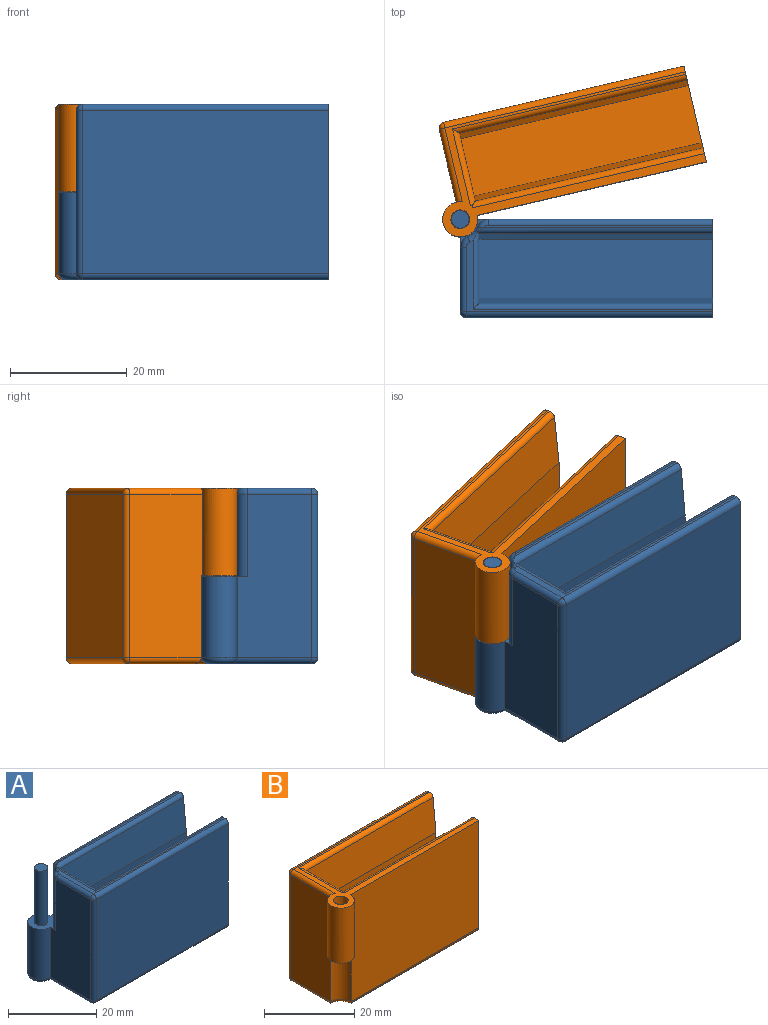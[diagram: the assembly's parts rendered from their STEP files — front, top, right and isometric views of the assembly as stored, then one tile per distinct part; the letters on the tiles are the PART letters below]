
ASSEMBLY  parts=2 mates=1
PART A: 36 faces, bbox 46.4x20x30 mm
  f0: plane 39.23x0.45mm, normal (0,0,1), area 17.3mm2, adj f7,f25,f27,f28
  f1: cylinder r=3.2mm len=14.05mm, axis (0,0,-1), area 35.1mm2, adj f13,f16,f17,f26
  f2: plane 28x12.8mm, normal (-1,0,0), area 333.1mm2, adj f12,f13,f16,f22,f32,f34
  f3: plane 42.2x28mm, normal (0,-1,0), area 1181.6mm2, adj f7,f20,f31,f34
  f4: plane 40x15mm, normal (0,1,0), area 600mm2, adj f5,f7,f11,f18
  f5: plane 24x11.9mm, normal (1,0,0), area 250.5mm2, adj f4,f6,f11,f18,f19,f23
  f6: plane 40x15mm, normal (0,-1,0), area 600mm2, adj f5,f7,f11,f19
  f7: plane 30x16.8mm, normal (1,0,0), area 240.3mm2, adj f0,f3,f4,f6,f8,f9,f10,f11
  f8: plane 40.2x28mm, normal (0,1,0), area 1100.3mm2, adj f7,f12,f13,f17,f28,f29
  f9: plane 42.2x12.22mm, normal (0,0,1), area 32.5mm2, adj f7,f20,f21,f22,f23,f24,f26
  f10: plane 45.2x17.8mm, normal (0,0,-1), area 636.8mm2, adj f7,f29,f30,f31,f32
  f11: plane 40x10.1mm, normal (0,0,1), area 404mm2, adj f4,f5,f6,f7
  f12: cylinder r=3mm len=13.95mm, axis (0,0,-1), area 197.2mm2, adj f2,f8,f13,f30
  f13: plane 7.8x7.8mm, normal (0,0,1), area 23mm2, adj f1,f2,f8,f12,f15,f16,f17
  f14: plane 3x3mm, normal (0,0,1), area 7.1mm2, adj f15
  f15: cylinder r=1.5mm len=15.05mm, axis (0,0,-1), area 141.8mm2, adj f13,f14
  f16: cylinder r=2mm len=14.05mm, axis (0,0,-1), area 33mm2, adj f1,f2,f13,f24
  f17: cylinder r=2mm len=14.05mm, axis (0,0,-1), area 33mm2, adj f1,f8,f13,f27
  f18: plane 40.01x9.1mm, normal (0,1,0.1), area 365.8mm2, adj f4,f5,f7,f21,f23
  f19: plane 40.01x9.1mm, normal (0,-1,0.1), area 365.8mm2, adj f5,f6,f7,f23,f25
  f20: cylinder r=1mm len=42.2mm, axis (-1,0,0), area 66.3mm2, adj f3,f7,f9,f35
  f21: cylinder r=1mm len=41mm, axis (1,0,0), area 59.4mm2, adj f7,f9,f18,f23
  f22: cylinder r=1mm len=11mm, axis (0,1,0), area 17.3mm2, adj f2,f9,f24,f35
  f23: cylinder r=1mm len=13.25mm, axis (0,-1,0), area 19.1mm2, adj f5,f9,f18,f19,f21,f25,f26
  f24: torus R=1mm, axis (0,0,1), area 3mm2, adj f9,f16,f22,f26
  f25: cylinder r=1mm len=40.34mm, axis (-1,0,0), area 58.8mm2, adj f0,f7,f19,f23,f26,f27
  f26: torus R=4.2mm, axis (0,0,1), area 3.4mm2, adj f1,f9,f23,f24,f25,f27
  f27: torus R=1mm, axis (0,0,1), area 3mm2, adj f0,f17,f25,f26,f28
  f28: cylinder r=1mm len=38.4mm, axis (1,0,0), area 60.3mm2, adj f0,f7,f8,f27
  f29: cylinder r=1mm len=41.47mm, axis (-1,0,0), area 63.8mm2, adj f7,f8,f10,f30
  f30: torus R=2mm, axis (0,0,1), area 20.7mm2, adj f10,f12,f29,f32
  f31: cylinder r=1mm len=42.2mm, axis (1,0,0), area 66.3mm2, adj f3,f7,f10,f33
  f32: cylinder r=1mm len=14.07mm, axis (0,-1,0), area 20.8mm2, adj f2,f10,f30,f33
  f33: sphere r=1mm, area 1.6mm2, adj f31,f32,f34
  f34: cylinder r=1mm len=28mm, axis (0,0,-1), area 44mm2, adj f2,f3,f33,f35
  f35: sphere r=1mm, area 1.6mm2, adj f20,f22,f34
PART B: 29 faces, bbox 46.2x19.8x30 mm
  f0: plane 30x16.8mm, normal (1,0,0), area 240.5mm2, adj f1,f7,f10,f11,f13,f14,f15,f16
  f1: plane 46.2x18.8mm, normal (0,0,1), area 112.7mm2, adj f0,f3,f4,f6,f7,f8,f18,f19
  f2: cylinder r=3.2mm len=14.05mm, axis (0,0,-1), area 70.6mm2, adj f5,f9,f22,f28
  f3: cylinder r=3mm len=0.59mm, axis (0,0,-1), area 0mm2, adj f1,f7,f8
  f4: cylinder r=3mm len=14.95mm, axis (0,0,-1), area 211.6mm2, adj f1,f5,f9,f19,f28
  f5: plane 6.2x6.2mm, normal (0,0,-1), area 21.2mm2, adj f2,f4,f6,f9,f28
  f6: cylinder r=1.6mm len=14.95mm, axis (0,0,-1), area 150.3mm2, adj f1,f5
  f7: cylinder r=1mm len=40.74mm, axis (-1,0,0), area 59.4mm2, adj f0,f1,f3,f8,f17
  f8: cylinder r=1mm len=13.65mm, axis (0,1,0), area 19.8mm2, adj f1,f3,f7,f12,f16,f17,f18
  f9: plane 28x12.8mm, normal (-1,0,0), area 355.6mm2, adj f2,f4,f5,f19,f24,f26
  f10: plane 42.2x28mm, normal (0,1,0), area 1181.6mm2, adj f0,f20,f23,f26
  f11: plane 40x15mm, normal (0,-1,0), area 600mm2, adj f0,f12,f15,f16
  f12: plane 24x11.9mm, normal (1,0,0), area 250.5mm2, adj f8,f11,f13,f15,f16,f17
  f13: plane 40x15mm, normal (0,1,0), area 600mm2, adj f0,f12,f15,f17
  f14: plane 42.2x14.8mm, normal (0,0,-1), area 618mm2, adj f0,f21,f22,f23,f24
  f15: plane 40x10.1mm, normal (0,0,1), area 404mm2, adj f0,f11,f12,f13
  f16: plane 40.01x9.1mm, normal (0,-1,0.1), area 365.8mm2, adj f0,f8,f11,f12,f18
  f17: plane 40.01x9.1mm, normal (0,1,0.1), area 365.8mm2, adj f0,f7,f8,f12,f13
  f18: cylinder r=1mm len=41mm, axis (1,0,0), area 59.4mm2, adj f0,f1,f8,f16
  f19: cylinder r=1mm len=12.97mm, axis (0,-1,0), area 20.2mm2, adj f1,f4,f9,f27
  f20: cylinder r=1mm len=42.2mm, axis (-1,0,0), area 66.3mm2, adj f0,f1,f10,f27
  f21: cylinder r=1mm len=40mm, axis (-1,0,0), area 62.3mm2, adj f0,f14,f22,f28
  f22: torus R=4.2mm, axis (0,0,1), area 7.6mm2, adj f2,f14,f21,f24
  f23: cylinder r=1mm len=42.2mm, axis (1,0,0), area 66.3mm2, adj f0,f10,f14,f25
  f24: cylinder r=1mm len=12.6mm, axis (0,1,0), area 19.3mm2, adj f9,f14,f22,f25
  f25: sphere r=1mm, area 1.6mm2, adj f23,f24,f26
  f26: cylinder r=1mm len=28mm, axis (0,0,-1), area 44mm2, adj f9,f10,f25,f27
  f27: sphere r=1mm, area 1.6mm2, adj f19,f20,f26
  f28: plane 40.2x29mm, normal (0,-1,0), area 1163mm2, adj f0,f1,f2,f4,f5,f21
PLACE A at identity
PLACE B rot(axis=(0,0,1),13.2deg) t=(0,0,0)mm
MATE revolute A.f15 <-> B.f3  axis (0,0,1) through (0,0,30)mm
